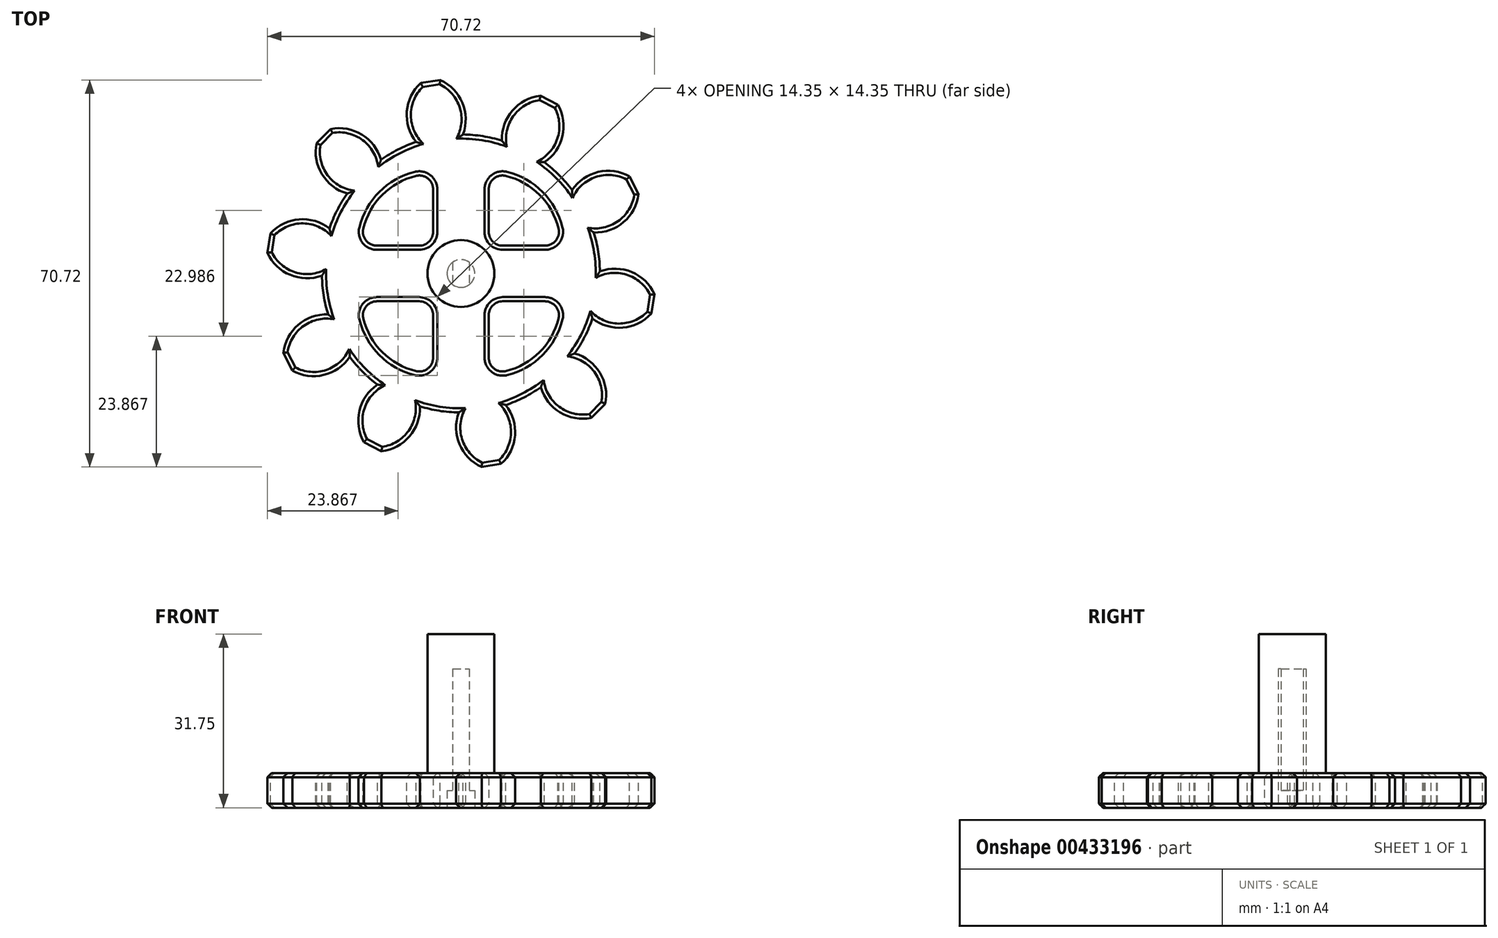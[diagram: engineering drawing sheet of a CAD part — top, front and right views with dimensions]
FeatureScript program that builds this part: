
annotation { "Feature Type Name" : "Feature", "Feature Type Description" : "" }
export const myFeature = defineFeature(function(context is Context, id is Id, definition is map)
    precondition{}
    {
        {
            var Q0;
            Q0=qCreatedBy(makeId("Top.planeOp"),FACE);
            var sketch = newSketch(context, id + "F0", { "sketchPlane" : qUnion([Q0])});
            skCircle(sketch, "E0", {"center": v(0, 0) * mm, "radius": 30.48 * mm, "construction": true});
            skSolve(sketch);
        }
        {
            var Q0;
            Q0=qCreatedBy(makeId("Top.planeOp"),FACE);
            var sketch = newSketch(context, id + "F1", { "sketchPlane" : qUnion([Q0])});
            skCircle(sketch, "E1", {"center": v(0, 0) * mm, "radius": 35.56 * mm, "construction": true});
            skCircle(sketch, "E2", {"center": v(0, 0) * mm, "radius": 31.75 * mm, "construction": true});
            skCircle(sketch, "E3", {"center": v(0, 0) * mm, "radius": 25.4 * mm, "construction": true});
            skLineSegment(sketch, "E4", {"start": v(0, 0) * mm, "end": v(0, 82.3) * mm, "construction": true});
            skLineSegment(sketch, "E5", {"start": v(0, 0) * mm, "end": v(-12.5, 78.88) * mm, "construction": true});
            skLineSegment(sketch, "E6", {"start": v(0, 31.75) * mm, "end": v(-65.71, 31.75) * mm, "construction": true});
            skLineSegment(sketch, "E7", {"start": v(0, 31.75) * mm, "end": v(-58.85, 5.55) * mm, "construction": true});
            skCircle(sketch, "E8", {"center": v(0, 31.75) * mm, "radius": 7.94 * mm, "construction": true});
            skCircle(sketch, "E9", {"center": v(0, 0) * mm, "radius": 29 * mm, "construction": true});
            skCircle(sketch, "E10", {"center": v(-7.06, 28.13) * mm, "radius": 7.94 * mm, "construction": true});
            skArc(sketch, "E11", {"start": v(0.39, 25.4) * mm, "mid": v(0.26, 31.2) * mm, "end": v(-3.78, 35.36) * mm});
            skArc(sketch, "E12.MirrorCS", {"start": v(-8.22, 24.03) * mm, "mid": v(-9.88, 29.59) * mm, "end": v(-7.33, 34.8) * mm});
            skLineSegment(sketch, "E13", {"start": v(-7.33, 34.8) * mm, "end": v(-3.78, 35.36) * mm});
            skArc(sketch, "E14", {"start": v(-8.22, 24.03) * mm, "mid": v(3.97, -25.09) * mm, "end": v(0.39, 25.4) * mm});
            skSolve(sketch);
        }
        {
            var Q0;
            Q0=qSketchRegion(id+"F1",true);
            var Q1;
            Q1=makeQuery(id+"Ffi0VH93psu6soF_0.opExtrude","CAP_FACE",FACE,{"disambiguationData":[OSD([sQuery(id+"F0.wireOp",EDGE,"E0")])],"isStart":true});
            extrude(context, id + "F2", {"entities" : qUnion([Q0]), "oppositeDirection" : true, "endBoundEntityFace" : qUnion([Q1]), "depth" : 6.35 * mm});
        }
        {
            var Q0;
            Q0=makeQuery(id+"F2.opExtrude","SWEPT_BODY",BODY,{"disambiguationData":[OSD([sQuery(id+"F1.wireOp",EDGE,"E11"),sQuery(id+"F1.wireOp",EDGE,"E12.MirrorCS"),sQuery(id+"F1.wireOp",EDGE,"E13"),sQuery(id+"F1.wireOp",EDGE,"ZPE7Z8ba-rLlS-d3gG-Tl0h-fifcE816pJjn")])]});
            var Q1;
            Q1=sQuery(id+"F0.wireOp",EDGE,"E0");
            circularPattern(context, id + "F3", {"operationType" : NewBodyOperationType.ADD, "entities" : qUnion([Q0]), "axis" : qUnion([Q1]), "angle" : 360 * degree, "instanceCount" : 10, "equalSpace" : true});
        }
        {
            var Q0;
            {var subQ0=makeQuery(id+"F2.opExtrude","CAP_FACE",FACE,{"disambiguationData":[OSD([sQuery(id+"F1.wireOp",EDGE,"E11"),sQuery(id+"F1.wireOp",EDGE,"E12.MirrorCS"),sQuery(id+"F1.wireOp",EDGE,"E13"),sQuery(id+"F1.wireOp",EDGE,"ZPE7Z8ba-rLlS-d3gG-Tl0h-fifcE816pJjn")])],"isStart":true});Q0=makeQuery(id+"F3.boolean.opBoolean","MERGE",FACE,{"derivedFrom":[makeQuery(id+"Ffi0VH93psu6soF_0.opExtrude","CAP_FACE",FACE,{"disambiguationData":[OSD([sQuery(id+"F0.wireOp",EDGE,"E0")])],"isStart":false}),subQ0,makeQuery(id+"F3.opPattern","COPY",FACE,{"derivedFrom":subQ0,"instanceName":"1"}),makeQuery(id+"F3.opPattern","COPY",FACE,{"derivedFrom":subQ0,"instanceName":"2"}),makeQuery(id+"F3.opPattern","COPY",FACE,{"derivedFrom":subQ0,"instanceName":"3"}),makeQuery(id+"F3.opPattern","COPY",FACE,{"derivedFrom":subQ0,"instanceName":"4"}),makeQuery(id+"F3.opPattern","COPY",FACE,{"derivedFrom":subQ0,"instanceName":"5"}),makeQuery(id+"F3.opPattern","COPY",FACE,{"derivedFrom":subQ0,"instanceName":"6"}),makeQuery(id+"F3.opPattern","COPY",FACE,{"derivedFrom":subQ0,"instanceName":"7"}),makeQuery(id+"F3.opPattern","COPY",FACE,{"derivedFrom":subQ0,"instanceName":"8"}),makeQuery(id+"F3.opPattern","COPY",FACE,{"derivedFrom":subQ0,"instanceName":"9"}),makeQuery(id+"F3.opPattern","COPY",FACE,{"derivedFrom":subQ0,"instanceName":"10"}),makeQuery(id+"F3.opPattern","COPY",FACE,{"derivedFrom":subQ0,"instanceName":"11"}),makeQuery(id+"F3.opPattern","COPY",FACE,{"derivedFrom":subQ0,"instanceName":"12"}),makeQuery(id+"F3.opPattern","COPY",FACE,{"derivedFrom":subQ0,"instanceName":"13"}),makeQuery(id+"F3.opPattern","COPY",FACE,{"derivedFrom":subQ0,"instanceName":"14"})]});}
            var sketch = newSketch(context, id + "F4", { "sketchPlane" : qUnion([Q0])});
            skLineSegment(sketch, "E15", {"start": v(-5.08, 5.08) * mm, "end": v(-18.22, 5.08) * mm});
            skLineSegment(sketch, "E16", {"start": v(-5.08, 5.08) * mm, "end": v(-5.08, 18.22) * mm});
            skArc(sketch, "E17", {"start": v(-5.08, 18.22) * mm, "mid": v(-14.37, 14.37) * mm, "end": v(-18.22, 5.08) * mm});
            skArc(sketch, "E18.1.0", {"start": v(-18.22, -5.08) * mm, "mid": v(-14.37, -14.37) * mm, "end": v(-5.08, -18.22) * mm});
            skLineSegment(sketch, "E18.1.1", {"start": v(-5.08, -5.08) * mm, "end": v(-18.22, -5.08) * mm});
            skLineSegment(sketch, "E18.1.2", {"start": v(-5.08, -5.08) * mm, "end": v(-5.08, -18.22) * mm});
            skArc(sketch, "E18.2.0", {"start": v(5.08, -18.22) * mm, "mid": v(14.37, -14.37) * mm, "end": v(18.22, -5.08) * mm});
            skLineSegment(sketch, "E18.2.1", {"start": v(5.08, -5.08) * mm, "end": v(5.08, -18.22) * mm});
            skLineSegment(sketch, "E18.2.2", {"start": v(5.08, -5.08) * mm, "end": v(18.22, -5.08) * mm});
            skArc(sketch, "E18.3.0", {"start": v(18.22, 5.08) * mm, "mid": v(14.37, 14.37) * mm, "end": v(5.08, 18.22) * mm});
            skLineSegment(sketch, "E18.3.1", {"start": v(5.08, 5.08) * mm, "end": v(18.22, 5.08) * mm});
            skLineSegment(sketch, "E18.3.2", {"start": v(5.08, 5.08) * mm, "end": v(5.08, 18.22) * mm});
            skPoint(sketch, "E18.center", {"position": v(0, 0) * mm});
            skSolve(sketch);
        }
        {
            var Q0;
            Q0=qSketchRegion(id+"F4",true);
            extrude(context, id + "F5", {"entities" : qUnion([Q0]), "operationType" : NewBodyOperationType.REMOVE, "endBound" : BoundingType.THROUGH_ALL, "oppositeDirection" : true, "depth" : 25.4 * mm});
        }
        {
            var Q0;
            Q0=makeQuery(id+"F5.boolean.opBoolean","COPY",EDGE,{"derivedFrom":makeQuery(id+"F5.opExtrude","SWEPT_EDGE",EDGE,{"disambiguationData":[OSD([sQuery(id+"F4.wireOp",EDGE,"E18.1.1"),sQuery(id+"F4.wireOp",EDGE,"E18.1.2")])]})});
            var Q1;
            Q1=makeQuery(id+"F5.boolean.opBoolean","COPY",EDGE,{"derivedFrom":makeQuery(id+"F5.opExtrude","SWEPT_EDGE",EDGE,{"disambiguationData":[OSD([sQuery(id+"F4.wireOp",EDGE,"E18.1.0"),sQuery(id+"F4.wireOp",EDGE,"E18.1.1")])]})});
            var Q2;
            Q2=makeQuery(id+"F5.boolean.opBoolean","COPY",EDGE,{"derivedFrom":makeQuery(id+"F5.opExtrude","SWEPT_EDGE",EDGE,{"disambiguationData":[OSD([sQuery(id+"F4.wireOp",EDGE,"E18.1.0"),sQuery(id+"F4.wireOp",EDGE,"E18.1.2")])]})});
            var Q3;
            Q3=makeQuery(id+"F5.boolean.opBoolean","COPY",EDGE,{"derivedFrom":makeQuery(id+"F5.opExtrude","SWEPT_EDGE",EDGE,{"disambiguationData":[OSD([sQuery(id+"F4.wireOp",EDGE,"E18.2.1"),sQuery(id+"F4.wireOp",EDGE,"E18.2.2")])]})});
            var Q4;
            Q4=makeQuery(id+"F5.boolean.opBoolean","COPY",EDGE,{"derivedFrom":makeQuery(id+"F5.opExtrude","SWEPT_EDGE",EDGE,{"disambiguationData":[OSD([sQuery(id+"F4.wireOp",EDGE,"E18.2.0"),sQuery(id+"F4.wireOp",EDGE,"E18.2.2")])]})});
            var Q5;
            Q5=makeQuery(id+"F5.boolean.opBoolean","COPY",EDGE,{"derivedFrom":makeQuery(id+"F5.opExtrude","SWEPT_EDGE",EDGE,{"disambiguationData":[OSD([sQuery(id+"F4.wireOp",EDGE,"E18.2.0"),sQuery(id+"F4.wireOp",EDGE,"E18.2.1")])]})});
            var Q6;
            Q6=makeQuery(id+"F5.boolean.opBoolean","COPY",EDGE,{"derivedFrom":makeQuery(id+"F5.opExtrude","SWEPT_EDGE",EDGE,{"disambiguationData":[OSD([sQuery(id+"F4.wireOp",EDGE,"E18.3.0"),sQuery(id+"F4.wireOp",EDGE,"E18.3.1")])]})});
            var Q7;
            Q7=makeQuery(id+"F5.boolean.opBoolean","COPY",EDGE,{"derivedFrom":makeQuery(id+"F5.opExtrude","SWEPT_EDGE",EDGE,{"disambiguationData":[OSD([sQuery(id+"F4.wireOp",EDGE,"E18.3.0"),sQuery(id+"F4.wireOp",EDGE,"E18.3.2")])]})});
            var Q8;
            Q8=makeQuery(id+"F5.boolean.opBoolean","COPY",EDGE,{"derivedFrom":makeQuery(id+"F5.opExtrude","SWEPT_EDGE",EDGE,{"disambiguationData":[OSD([sQuery(id+"F4.wireOp",EDGE,"E18.3.1"),sQuery(id+"F4.wireOp",EDGE,"E18.3.2")])]})});
            var Q9;
            Q9=makeQuery(id+"F5.boolean.opBoolean","COPY",EDGE,{"derivedFrom":makeQuery(id+"F5.opExtrude","SWEPT_EDGE",EDGE,{"disambiguationData":[OSD([sQuery(id+"F4.wireOp",EDGE,"E15"),sQuery(id+"F4.wireOp",EDGE,"E16")])]})});
            var Q10;
            Q10=makeQuery(id+"F5.boolean.opBoolean","COPY",EDGE,{"derivedFrom":makeQuery(id+"F5.opExtrude","SWEPT_EDGE",EDGE,{"disambiguationData":[OSD([sQuery(id+"F4.wireOp",EDGE,"E16"),sQuery(id+"F4.wireOp",EDGE,"E17")])]})});
            var Q11;
            Q11=makeQuery(id+"F5.boolean.opBoolean","COPY",EDGE,{"derivedFrom":makeQuery(id+"F5.opExtrude","SWEPT_EDGE",EDGE,{"disambiguationData":[OSD([sQuery(id+"F4.wireOp",EDGE,"E15"),sQuery(id+"F4.wireOp",EDGE,"E17")])]})});
            fillet(context, id + "F6", {"entities" : qUnion([Q0, Q1, Q2, Q3, Q4, Q5, Q6, Q7, Q8, Q9, Q10, Q11]), "radius" : 2.54 * mm, "tangentPropagation" : true, "allowEdgeOverflow" : false});
        }
        {
            var Q0;
            {var subQ0=makeQuery(id+"F2.opExtrude","CAP_FACE",FACE,{"disambiguationData":[OSD([sQuery(id+"F1.wireOp",EDGE,"E11"),sQuery(id+"F1.wireOp",EDGE,"E12.MirrorCS"),sQuery(id+"F1.wireOp",EDGE,"E13"),sQuery(id+"F1.wireOp",EDGE,"E14")])],"isStart":true});Q0=makeQuery(id+"F3.boolean.opBoolean","MERGE",FACE,{"derivedFrom":[subQ0,makeQuery(id+"F3.opPattern","COPY",FACE,{"derivedFrom":subQ0,"instanceName":"1"}),makeQuery(id+"F3.opPattern","COPY",FACE,{"derivedFrom":subQ0,"instanceName":"2"}),makeQuery(id+"F3.opPattern","COPY",FACE,{"derivedFrom":subQ0,"instanceName":"3"}),makeQuery(id+"F3.opPattern","COPY",FACE,{"derivedFrom":subQ0,"instanceName":"4"}),makeQuery(id+"F3.opPattern","COPY",FACE,{"derivedFrom":subQ0,"instanceName":"5"}),makeQuery(id+"F3.opPattern","COPY",FACE,{"derivedFrom":subQ0,"instanceName":"6"}),makeQuery(id+"F3.opPattern","COPY",FACE,{"derivedFrom":subQ0,"instanceName":"7"}),makeQuery(id+"F3.opPattern","COPY",FACE,{"derivedFrom":subQ0,"instanceName":"8"}),makeQuery(id+"F3.opPattern","COPY",FACE,{"derivedFrom":subQ0,"instanceName":"9"})]});}
            var Q1;
            {var subQ0=makeQuery(id+"F2.opExtrude","CAP_FACE",FACE,{"disambiguationData":[OSD([sQuery(id+"F1.wireOp",EDGE,"E11"),sQuery(id+"F1.wireOp",EDGE,"E12.MirrorCS"),sQuery(id+"F1.wireOp",EDGE,"E13"),sQuery(id+"F1.wireOp",EDGE,"E14")])],"isStart":false});Q1=makeQuery(id+"F3.boolean.opBoolean","MERGE",FACE,{"derivedFrom":[subQ0,makeQuery(id+"F3.opPattern","COPY",FACE,{"derivedFrom":subQ0,"instanceName":"1"}),makeQuery(id+"F3.opPattern","COPY",FACE,{"derivedFrom":subQ0,"instanceName":"2"}),makeQuery(id+"F3.opPattern","COPY",FACE,{"derivedFrom":subQ0,"instanceName":"3"}),makeQuery(id+"F3.opPattern","COPY",FACE,{"derivedFrom":subQ0,"instanceName":"4"}),makeQuery(id+"F3.opPattern","COPY",FACE,{"derivedFrom":subQ0,"instanceName":"5"}),makeQuery(id+"F3.opPattern","COPY",FACE,{"derivedFrom":subQ0,"instanceName":"6"}),makeQuery(id+"F3.opPattern","COPY",FACE,{"derivedFrom":subQ0,"instanceName":"7"}),makeQuery(id+"F3.opPattern","COPY",FACE,{"derivedFrom":subQ0,"instanceName":"8"}),makeQuery(id+"F3.opPattern","COPY",FACE,{"derivedFrom":subQ0,"instanceName":"9"})]});}
            chamfer(context, id + "F7", {"entities" : qUnion([Q0, Q1]), "width" : 0.76 * mm, "tangentPropagation" : true});
        }
        {
            var Q0;
            {var subQ0=makeQuery(id+"F2.opExtrude","CAP_FACE",FACE,{"disambiguationData":[OSD([sQuery(id+"F1.wireOp",EDGE,"E11"),sQuery(id+"F1.wireOp",EDGE,"E12.MirrorCS"),sQuery(id+"F1.wireOp",EDGE,"E13"),sQuery(id+"F1.wireOp",EDGE,"E14")])],"isStart":true});Q0=makeQuery(id+"F3.boolean.opBoolean","MERGE",FACE,{"derivedFrom":[subQ0,makeQuery(id+"F3.opPattern","COPY",FACE,{"derivedFrom":subQ0,"instanceName":"1"}),makeQuery(id+"F3.opPattern","COPY",FACE,{"derivedFrom":subQ0,"instanceName":"2"}),makeQuery(id+"F3.opPattern","COPY",FACE,{"derivedFrom":subQ0,"instanceName":"3"}),makeQuery(id+"F3.opPattern","COPY",FACE,{"derivedFrom":subQ0,"instanceName":"4"}),makeQuery(id+"F3.opPattern","COPY",FACE,{"derivedFrom":subQ0,"instanceName":"5"}),makeQuery(id+"F3.opPattern","COPY",FACE,{"derivedFrom":subQ0,"instanceName":"6"}),makeQuery(id+"F3.opPattern","COPY",FACE,{"derivedFrom":subQ0,"instanceName":"7"}),makeQuery(id+"F3.opPattern","COPY",FACE,{"derivedFrom":subQ0,"instanceName":"8"}),makeQuery(id+"F3.opPattern","COPY",FACE,{"derivedFrom":subQ0,"instanceName":"9"})]});}
            var sketch = newSketch(context, id + "F8", { "sketchPlane" : qUnion([Q0])});
            skCircle(sketch, "E19", {"center": v(0, 0) * mm, "radius": 6.1 * mm});
            skSolve(sketch);
        }
        {
            var Q0;
            Q0 = qSketchRegion(id + "F8", true);
            extrude(context, id + "F9", {"entities" : qUnion([Q0]), "operationType" : NewBodyOperationType.ADD, "depth" : 25.4 * mm});
        }
        {
            var Q0;
            {var subQ0=makeQuery(id+"F2.opExtrude","CAP_FACE",FACE,{"disambiguationData":[OSD([sQuery(id+"F1.wireOp",EDGE,"E11"),sQuery(id+"F1.wireOp",EDGE,"E12.MirrorCS"),sQuery(id+"F1.wireOp",EDGE,"E13"),sQuery(id+"F1.wireOp",EDGE,"E14")])],"isStart":false});Q0=makeQuery(id+"F3.boolean.opBoolean","MERGE",FACE,{"derivedFrom":[subQ0,makeQuery(id+"F3.opPattern","COPY",FACE,{"derivedFrom":subQ0,"instanceName":"1"}),makeQuery(id+"F3.opPattern","COPY",FACE,{"derivedFrom":subQ0,"instanceName":"2"}),makeQuery(id+"F3.opPattern","COPY",FACE,{"derivedFrom":subQ0,"instanceName":"3"}),makeQuery(id+"F3.opPattern","COPY",FACE,{"derivedFrom":subQ0,"instanceName":"4"}),makeQuery(id+"F3.opPattern","COPY",FACE,{"derivedFrom":subQ0,"instanceName":"5"}),makeQuery(id+"F3.opPattern","COPY",FACE,{"derivedFrom":subQ0,"instanceName":"6"}),makeQuery(id+"F3.opPattern","COPY",FACE,{"derivedFrom":subQ0,"instanceName":"7"}),makeQuery(id+"F3.opPattern","COPY",FACE,{"derivedFrom":subQ0,"instanceName":"8"}),makeQuery(id+"F3.opPattern","COPY",FACE,{"derivedFrom":subQ0,"instanceName":"9"})]});}
            var sketch = newSketch(context, id + "F10", { "sketchPlane" : qUnion([Q0])});
            skArc(sketch, "E20", {"start": v(-1.52, -2.03) * mm, "mid": v(0, -2.54) * mm, "end": v(1.52, -2.03) * mm});
            skLineSegment(sketch, "E21", {"start": v(1.52, 2.03) * mm, "end": v(1.52, -2.03) * mm});
            skLineSegment(sketch, "E22", {"start": v(-1.52, 2.03) * mm, "end": v(-1.52, -2.03) * mm});
            skArc(sketch, "E23.trimOffspring", {"start": v(1.52, 2.03) * mm, "mid": v(0, 2.54) * mm, "end": v(-1.52, 2.03) * mm});
            skSolve(sketch);
        }
        {
            var Q0;
            Q0=qSketchRegion(id+"F10",true);
            extrude(context, id + "F11", {"entities" : qUnion([Q0]), "operationType" : NewBodyOperationType.REMOVE, "oppositeDirection" : true, "depth" : 25.4 * mm});
        }
        {
            var Q0;
            {var subQ0=makeQuery(id+"F2.opExtrude","CAP_FACE",FACE,{"disambiguationData":[OSD([sQuery(id+"F1.wireOp",EDGE,"E11"),sQuery(id+"F1.wireOp",EDGE,"E12.MirrorCS"),sQuery(id+"F1.wireOp",EDGE,"E13"),sQuery(id+"F1.wireOp",EDGE,"E14")])],"isStart":false});Q0=makeQuery(id+"F3.boolean.opBoolean","MERGE",FACE,{"derivedFrom":[subQ0,makeQuery(id+"F3.opPattern","COPY",FACE,{"derivedFrom":subQ0,"instanceName":"1"}),makeQuery(id+"F3.opPattern","COPY",FACE,{"derivedFrom":subQ0,"instanceName":"2"}),makeQuery(id+"F3.opPattern","COPY",FACE,{"derivedFrom":subQ0,"instanceName":"3"}),makeQuery(id+"F3.opPattern","COPY",FACE,{"derivedFrom":subQ0,"instanceName":"4"}),makeQuery(id+"F3.opPattern","COPY",FACE,{"derivedFrom":subQ0,"instanceName":"5"}),makeQuery(id+"F3.opPattern","COPY",FACE,{"derivedFrom":subQ0,"instanceName":"6"}),makeQuery(id+"F3.opPattern","COPY",FACE,{"derivedFrom":subQ0,"instanceName":"7"}),makeQuery(id+"F3.opPattern","COPY",FACE,{"derivedFrom":subQ0,"instanceName":"8"}),makeQuery(id+"F3.opPattern","COPY",FACE,{"derivedFrom":subQ0,"instanceName":"9"})]});}
            var sketch = newSketch(context, id + "F12", { "sketchPlane" : qUnion([Q0])});
            skCircle(sketch, "E24", {"center": v(0, 0) * mm, "radius": 2.54 * mm});
            skSolve(sketch);
        }
        {
            var Q0;
            Q0 = qSketchRegion(id + "F12", true);
            extrude(context, id + "F13", {"entities" : qUnion([Q0]), "operationType" : NewBodyOperationType.REMOVE, "oppositeDirection" : true, "depth" : 3.17 * mm, "offsetDistance" : 25.4 * mm});
        }
    });
